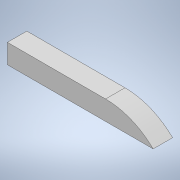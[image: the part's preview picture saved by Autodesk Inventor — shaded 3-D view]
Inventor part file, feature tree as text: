
AUTODESK INVENTOR PART (.ipt)
format: ipt  version: 2021 (Build 250183000, 183)  size: 104,960 bytes
history: native  units: in
note: dims shown in document units (in); Inventor stores cm internally (conversion verified against a paired STEP export)
features: extrude x2, sketch x2, plane x1, fillet x1
ambient origin geometry x8: Origin, YZ Plane, XZ Plane, XY Plane, X Axis, Y Axis, Z Axis, Center Point
bodies: Solid1 (feature_tree)
feature tree (6):
  extrude  "Extrusion1"  Depth=0.0472in
  plane  "Work Plane1"
  extrude  "Extrusion2"  TaperAngle=0.0deg  [1 undecoded]
  fillet  "Fillet1"  Radius=0.0472in
  sketch  "Sketch1"  dims[d0=0.0472in d1=0.0472in]
  sketch  "Sketch2"  dims[d2=0.3543in d3=0.0in d4=0.0in d5=0.0472in d6=0.3543in d7=0.0in d8=0.1654in]
note: 1 required parameter value undecoded (feature->parameter linkage not recoverable at this tier; creation-order binding heuristic only, values carry confidence <= 0.55)
